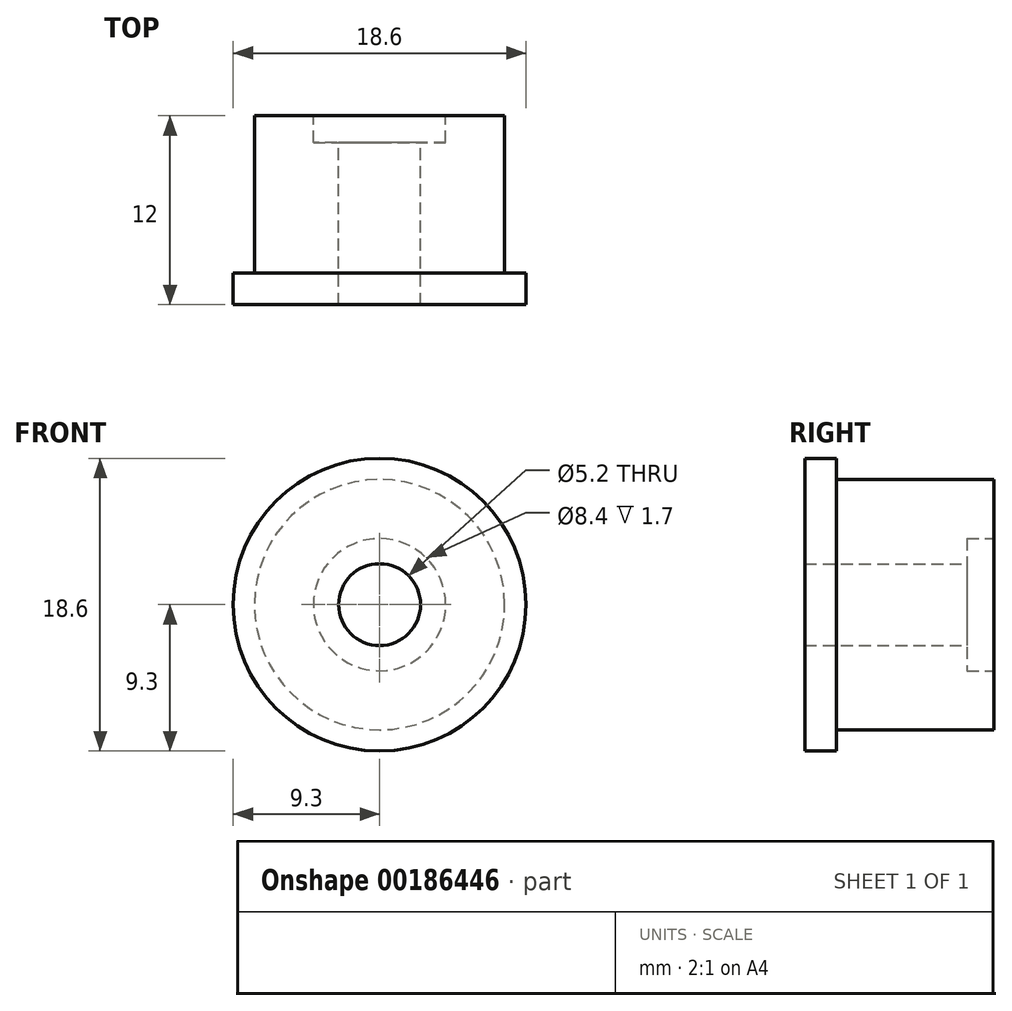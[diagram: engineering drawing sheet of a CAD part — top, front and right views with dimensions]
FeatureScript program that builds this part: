
annotation { "Feature Type Name" : "Feature", "Feature Type Description" : "" }
export const myFeature = defineFeature(function(context is Context, id is Id, definition is map)
    precondition{}
    {
        {
            var Q0;
            Q0=qCreatedBy(makeId("Right.planeOp"),FACE);
            var sketch = newSketch(context, id + "F0", { "sketchPlane" : qUnion([Q0])});
            skLineSegment(sketch, "E0", {"start": v(11.47, 0) * mm, "end": v(0, 0) * mm, "construction": true});
            skLineSegment(sketch, "E1", {"start": v(10.3, 2.6) * mm, "end": v(0, 2.6) * mm});
            skLineSegment(sketch, "E2", {"start": v(10.3, 2.6) * mm, "end": v(10.3, 4.2) * mm});
            skLineSegment(sketch, "E3", {"start": v(12, 4.2) * mm, "end": v(10.3, 4.2) * mm});
            skLineSegment(sketch, "E4", {"start": v(12, 4.2) * mm, "end": v(12, 7.95) * mm});
            skLineSegment(sketch, "E5", {"start": v(2, 7.95) * mm, "end": v(12, 7.95) * mm});
            skLineSegment(sketch, "E6", {"start": v(2, 7.95) * mm, "end": v(2, 9.3) * mm});
            skLineSegment(sketch, "E7", {"start": v(0, 9.3) * mm, "end": v(2, 9.3) * mm});
            skLineSegment(sketch, "E8", {"start": v(0, 9.3) * mm, "end": v(0, 2.6) * mm});
            skSolve(sketch);
        }
        {
            var Q0;
            Q0=makeQuery(id+"F0.imprint","IMPRINT",FACE,{"disambiguationData":[TD([[makeQuery(id+"F0.imprint","IMPRINT",EDGE,{"derivedFrom":sQuery(id+"F0.wireOp",EDGE,"E1")}),-1.0]])]});
            var Q1;
            Q1=sQuery(id+"F0.wireOp",EDGE,"E0");
            revolve(context, id + "F1", {"entities" : qUnion([Q0]), "axis" : qUnion([Q1]), "revolveType" : RevolveType.FULL});
        }
    });
